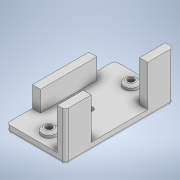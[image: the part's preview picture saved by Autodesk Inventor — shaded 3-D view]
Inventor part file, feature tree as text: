
AUTODESK INVENTOR PART (.ipt)
format: ipt  version: 2022 (Build 260153000, 153)  size: 227,328 bytes
history: native  units: in
note: dims shown in document units (in); Inventor stores cm internally (conversion verified against a paired STEP export)
features: extrude x8, sketch x8, fillet x2, chamfer x1
ambient origin geometry x8: Origin, YZ Plane, XZ Plane, XY Plane, X Axis, Y Axis, Z Axis, Center Point
bodies: Solid1 (feature_tree)
feature tree (19):
  extrude  "Extrusion1"  Depth=2.6378in
  extrude  "Extrusion2"  Depth=0.1969in
  fillet  "Fillet2"  Radius=0.8268in
  extrude  "Extrusion6"  Depth=1.0in
  fillet  "Fillet3"  Radius=1.0in
  extrude  "Extrusion8"  Depth=0.1969in
  chamfer  "Chamfer1"  Distance=1.0in
  extrude  "Extrusion9"  Depth=0.0787in
  extrude  "Extrusion10"  Depth=0.3406in
  extrude  "Extrusion11"  Depth=0.0787in TaperAngle=45.0deg
  extrude  "Extrusion12"  Depth=0.0197in
  sketch  "Sketch1"  dims[d0=1.4331in d1=2.6378in]
  sketch  "Sketch2"  dims[d2=0.1969in d3=0.0in d4=0.1969in d5=0.8268in]
  sketch  "Sketch6"  dims[d6=0.1969in d7=0.8268in d8=1.0in d9=0.0in]
  sketch  "Sketch8"  dims[d25=0.0787in d26=0.1969in]
  sketch  "Sketch9"  dims[d27=0.9449in d28=1.0in d29=0.0in]
  sketch  "Sketch10"  dims[d36=0.0787in d37=0.3406in]
  sketch  "Sketch11"  dims[d38=0.3406in d39=0.3406in]
  sketch  "Sketch12"  dims[d40=0.1181in d41=0.0in d42=0.0591in d43=0.0787in d44=45.0deg d45=0.1575in d46=0.1575in d47=0.1575in d48=0.7874in d49=0.0in d50=0.2362in d51=0.2362in d52=0.2362in d53=0.0984in d54=0.0in d55=1.378in d56=1.9685in d57=0.0in d58=0.1969in d59=0.5in d60=0.0in d10=0.0197in d11=0.0344in d13=0.0197in d14=0.0344in d15=0.0197in d16=0.0344in]
